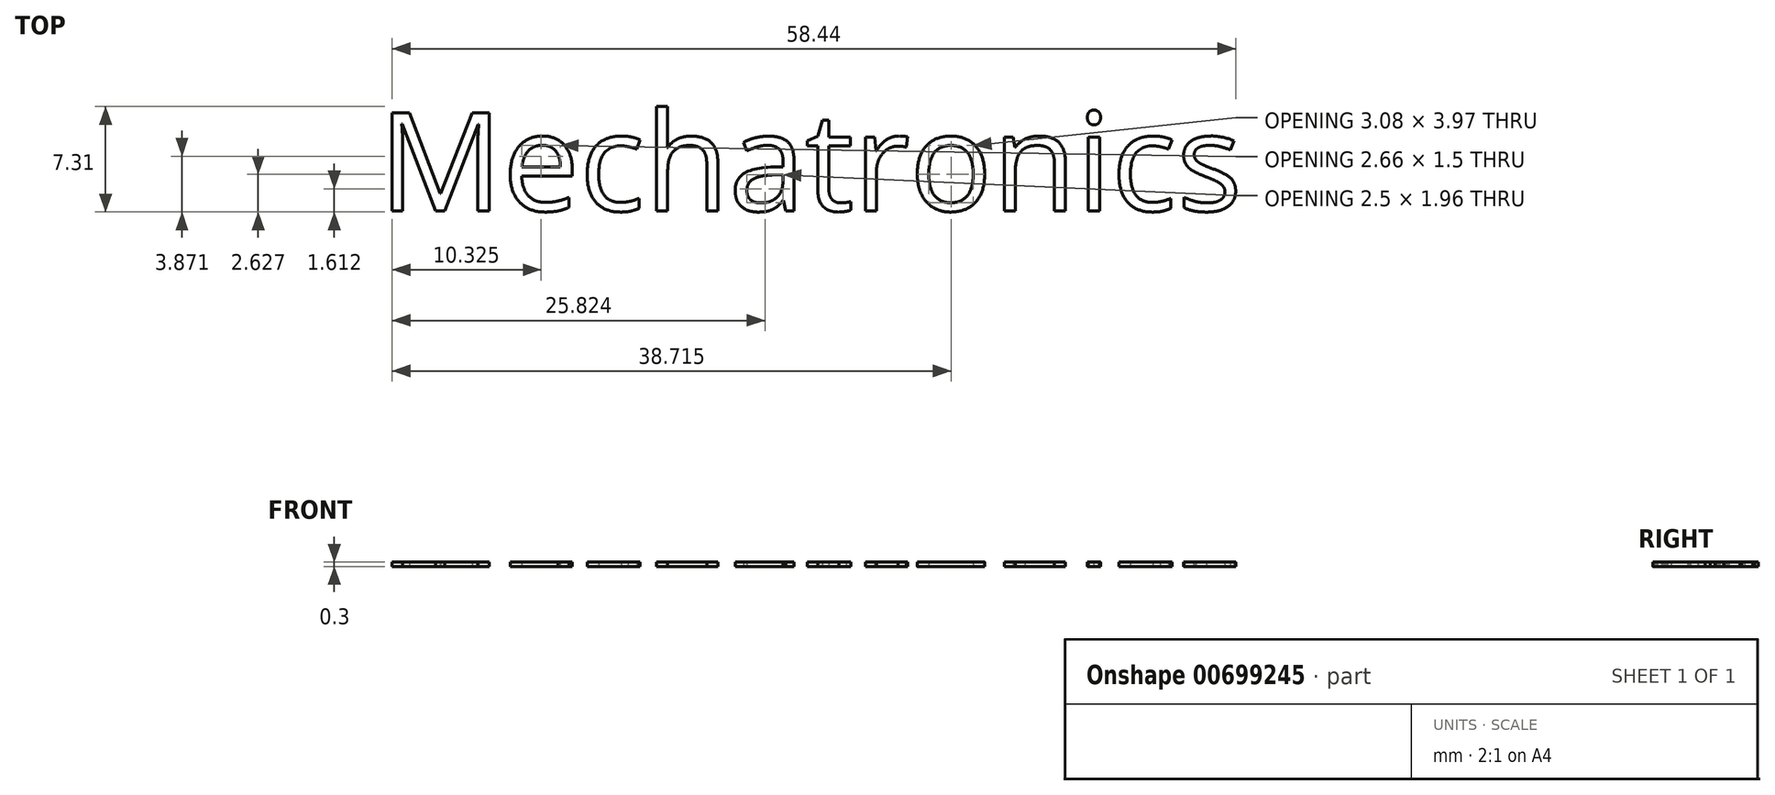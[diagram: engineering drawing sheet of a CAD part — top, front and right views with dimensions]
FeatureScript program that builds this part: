
annotation { "Feature Type Name" : "Feature", "Feature Type Description" : "" }
export const myFeature = defineFeature(function(context is Context, id is Id, definition is map)
    precondition{}
    {
        {
            var Q0;
            Q0=qCreatedBy(makeId("Top.planeOp"),FACE);
            var sketch = newSketch(context, id + "F0", { "sketchPlane" : qUnion([Q0])});
            skText(sketch, "E0", { "text": "Mechatronics", "fontName": "OpenSans-Regular.ttf"});
            const initialGuessF0  = {"E0": [-0.0053, -0.00347, 1, 0, 0.00684]};
            skSetInitialGuess(sketch, initialGuessF0);
            skSolve(sketch);
        }
        {
            var Q0;
            Q0 = qSketchRegion(id + "F0", true);
            extrude(context, id + "F1", {"entities" : qUnion([Q0]), "depth" : .3 * mm, "offsetDistance" : 25.4 * mm});
        }
    });
